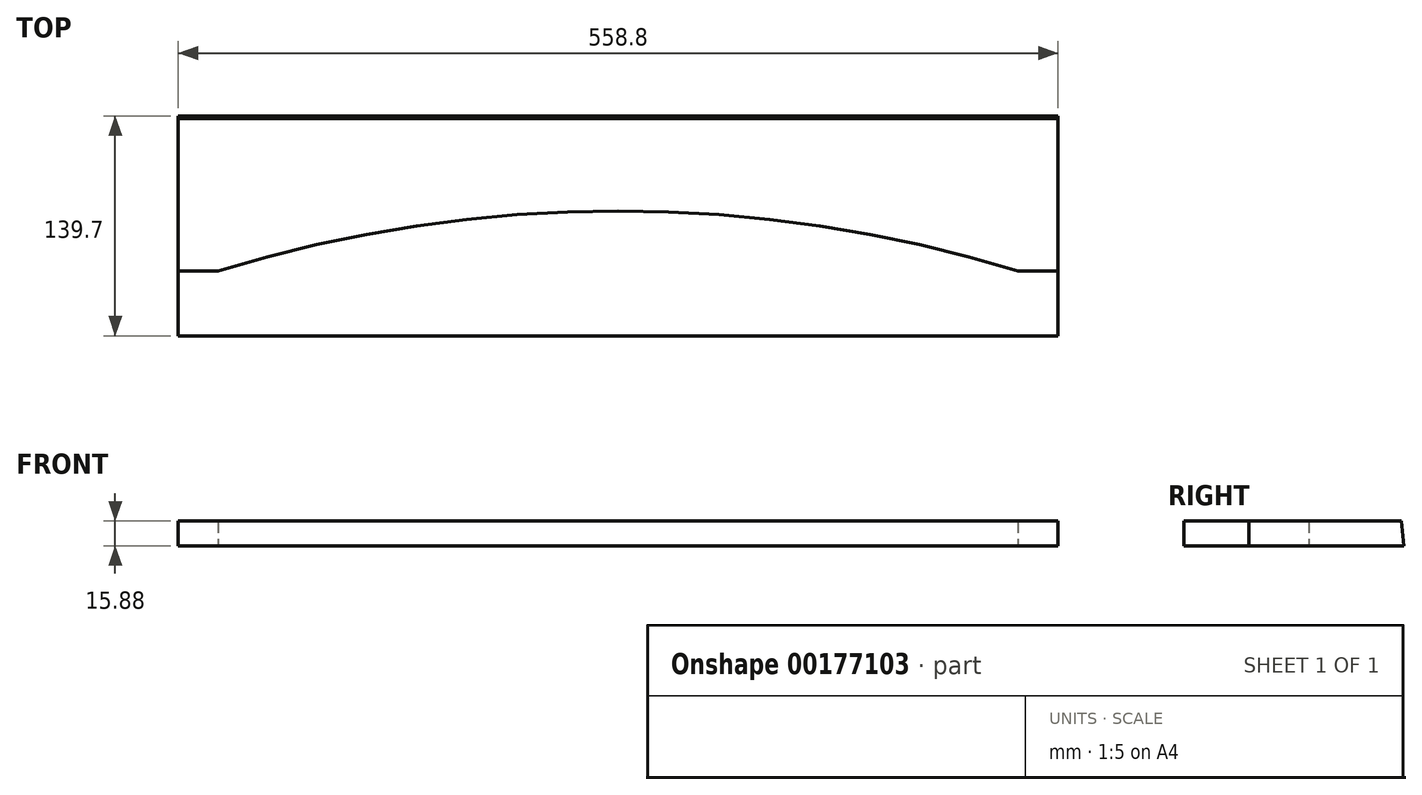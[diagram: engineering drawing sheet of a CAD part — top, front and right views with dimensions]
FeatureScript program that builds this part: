
annotation { "Feature Type Name" : "Feature", "Feature Type Description" : "" }
export const myFeature = defineFeature(function(context is Context, id is Id, definition is map)
    precondition{}
    {
        {
            var Q0;
            Q0=qCreatedBy(makeId("Top.planeOp"),FACE);
            var sketch = newSketch(context, id + "F0", { "sketchPlane" : qUnion([Q0])});
            skLineSegment(sketch, "E0", {"start": v(0, 0) * mm, "end": v(558.8, 0) * mm});
            skLineSegment(sketch, "E1", {"start": v(0, 0) * mm, "end": v(0, -98.43) * mm});
            skLineSegment(sketch, "E2", {"start": v(0, -98.42) * mm, "end": v(0, -139.7) * mm});
            skLineSegment(sketch, "E3", {"start": v(0, -139.7) * mm, "end": v(558.8, -139.7) * mm});
            skLineSegment(sketch, "E4", {"start": v(558.8, -139.7) * mm, "end": v(558.8, -98.42) * mm});
            skLineSegment(sketch, "E5", {"start": v(558.8, -98.42) * mm, "end": v(558.8, 0) * mm});
            skLineSegment(sketch, "E6", {"start": v(0, -98.43) * mm, "end": v(25.4, -98.43) * mm});
            skArc(sketch, "E7", {"start": v(533.4, -98.42) * mm, "mid": v(279.4, -60.32) * mm, "end": v(25.4, -98.42) * mm});
            skLineSegment(sketch, "E8", {"start": v(279.4, 0) * mm, "end": v(279.4, -60.33) * mm, "construction": true});
            skLineSegment(sketch, "E9", {"start": v(533.4, -98.42) * mm, "end": v(558.8, -98.42) * mm});
            skSolve(sketch);
        }
        {
            var Q0;
            Q0=makeQuery(id+"F0.imprint","IMPRINT",FACE,{"disambiguationData":[TD([[makeQuery(id+"F0.imprint","IMPRINT",EDGE,{"derivedFrom":sQuery(id+"F0.wireOp",EDGE,"E0")}),-1.0]])]});
            extrude(context, id + "F1", {"entities" : qUnion([Q0]), "depth" : 15.88 * mm});
        }
        {
            var Q0;
            Q0=makeQuery(id+"F0.imprint","IMPRINT",FACE,{"disambiguationData":[TD([[makeQuery(id+"F0.imprint","IMPRINT",EDGE,{"derivedFrom":sQuery(id+"F0.wireOp",EDGE,"E2")}),1.0]])]});
            extrude(context, id + "F2", {"entities" : qUnion([Q0]), "depth" : 15.88 * mm});
        }
        {
            var Q0;
            Q0=makeQuery(id+"F1.opExtrude","CAP_EDGE",EDGE,{"disambiguationData":[OSD([sQuery(id+"F0.wireOp",EDGE,"E0")])],"isStart":false});
            chamfer(context, id + "F3", {"entities" : qUnion([Q0]), "chamferType" : ChamferType.OFFSET_ANGLE, "width" : 15.88 * mm, "oppositeDirection" : false, "angle" : 6 * degree, "tangentPropagation" : true});
        }
    });
